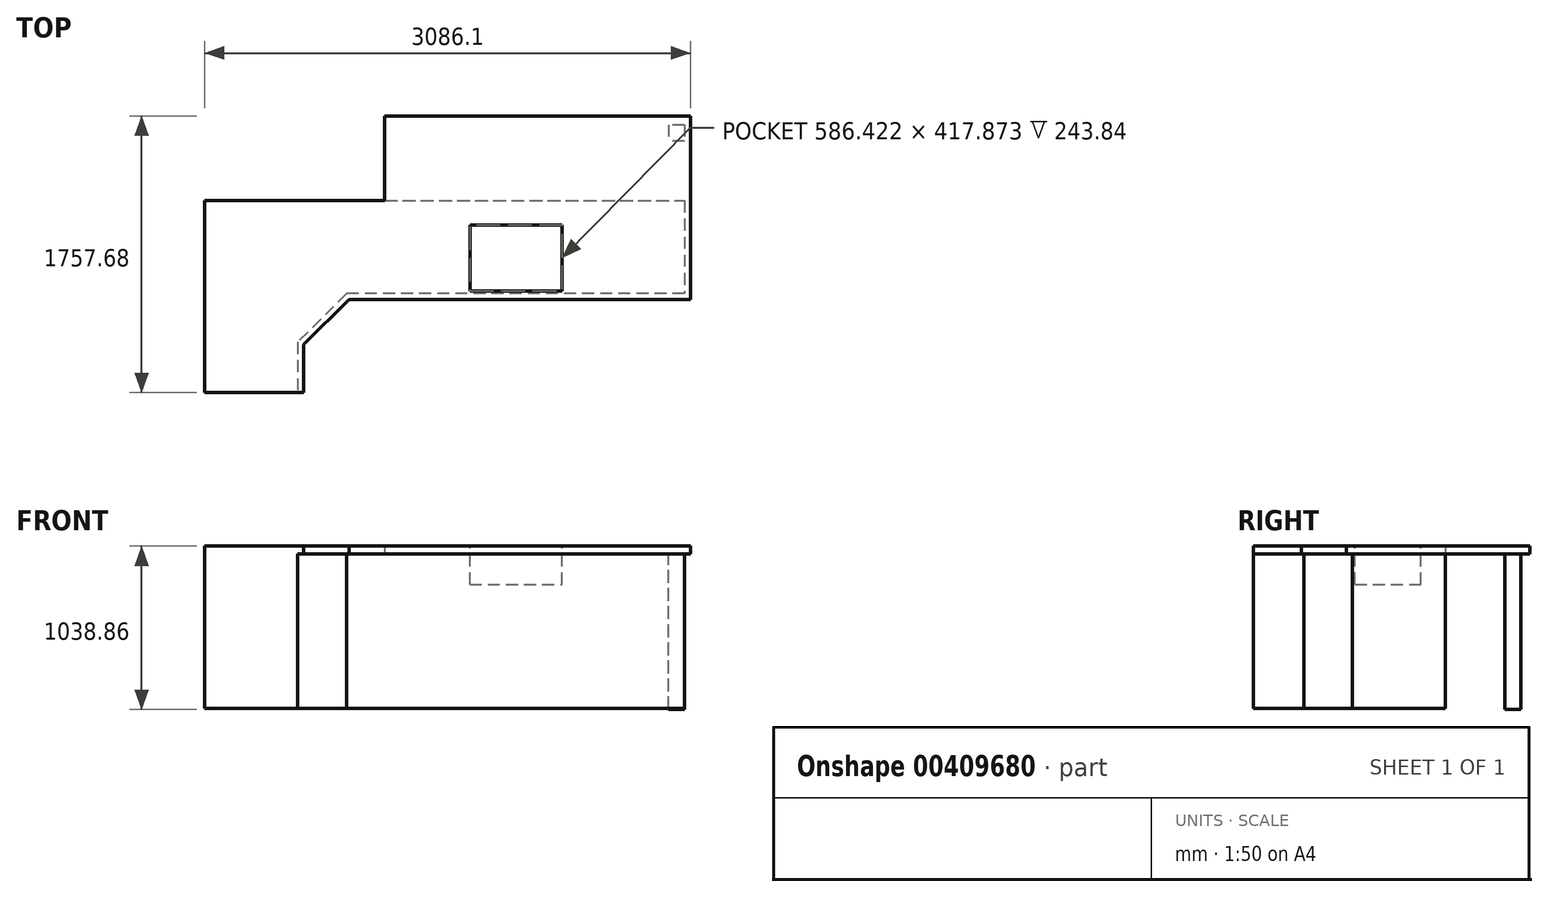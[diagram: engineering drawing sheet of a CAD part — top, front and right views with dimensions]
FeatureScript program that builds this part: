
annotation { "Feature Type Name" : "Feature", "Feature Type Description" : "" }
export const myFeature = defineFeature(function(context is Context, id is Id, definition is map)
    precondition{}
    {
        {
            var Q0;
            Q0=qCreatedBy(makeId("Top.planeOp"),FACE);
            var sketch = newSketch(context, id + "F0", { "sketchPlane" : qUnion([Q0])});
            skLineSegment(sketch, "E0.bottom", {"start": v(0, 0) * mm, "end": v(628.65, 0) * mm});
            skLineSegment(sketch, "E0.top", {"start": v(0, 1219.2) * mm, "end": v(1143, 1219.2) * mm});
            skLineSegment(sketch, "E0.left", {"start": v(0, 0) * mm, "end": v(0, 1219.2) * mm});
            skLineSegment(sketch, "E1", {"start": v(628.65, 0) * mm, "end": v(628.65, 304.8) * mm});
            skLineSegment(sketch, "E2", {"start": v(628.65, 304.8) * mm, "end": v(917.63, 590.55) * mm});
            skLineSegment(sketch, "E3", {"start": v(917.63, 590.55) * mm, "end": v(3086.1, 590.55) * mm});
            skLineSegment(sketch, "E4", {"start": v(1143, 1219.2) * mm, "end": v(1143, 1524) * mm});
            skLineSegment(sketch, "E5", {"start": v(1143, 1524) * mm, "end": v(3086.1, 1524) * mm});
            skLineSegment(sketch, "E6", {"start": v(3086.1, 1524) * mm, "end": v(3086.1, 590.55) * mm});
            skSolve(sketch);
        }
        {
            var Q0;
            Q0=makeQuery(id+"F0.imprint","IMPRINT",FACE,{"disambiguationData":[TD([[makeQuery(id+"F0.imprint","IMPRINT",EDGE,{"derivedFrom":sQuery(id+"F0.wireOp",EDGE,"E0.bottom")}),1.0]])]});
            extrude(context, id + "F1", {"entities" : qUnion([Q0]), "depth" : 50.8 * mm});
        }
        {
            var Q0;
            Q0=makeQuery(id+"F1.opExtrude","CAP_FACE",FACE,{"disambiguationData":[OSD([sQuery(id+"F0.wireOp",EDGE,"E0.bottom"),sQuery(id+"F0.wireOp",EDGE,"E0.top"),sQuery(id+"F0.wireOp",EDGE,"E0.left"),sQuery(id+"F0.wireOp",EDGE,"E1"),sQuery(id+"F0.wireOp",EDGE,"E2"),sQuery(id+"F0.wireOp",EDGE,"E3"),sQuery(id+"F0.wireOp",EDGE,"E4"),sQuery(id+"F0.wireOp",EDGE,"E5"),sQuery(id+"F0.wireOp",EDGE,"E6")])],"isStart":true});
            var sketch = newSketch(context, id + "F2", { "sketchPlane" : qUnion([Q0])});
            skLineSegment(sketch, "E7", {"start": v(1143, -1219.2) * mm, "end": v(3048, -1219.2) * mm});
            skLineSegment(sketch, "E8", {"start": v(3048, -1219.2) * mm, "end": v(3048, -628.65) * mm});
            skLineSegment(sketch, "E9", {"start": v(3048, -628.65) * mm, "end": v(901.97, -628.65) * mm});
            skLineSegment(sketch, "E10", {"start": v(901.97, -628.65) * mm, "end": v(590.55, -320.7) * mm});
            skLineSegment(sketch, "E11", {"start": v(590.55, -320.7) * mm, "end": v(590.55, 0) * mm});
            skLineSegment(sketch, "E12", {"start": v(590.55, 0) * mm, "end": v(0, 0) * mm});
            skLineSegment(sketch, "E13", {"start": v(0, 0) * mm, "end": v(0, -1219.2) * mm});
            skLineSegment(sketch, "E14", {"start": v(0, -1219.2) * mm, "end": v(1143, -1219.2) * mm});
            skSolve(sketch);
        }
        {
            var Q0;
            Q0=makeQuery(id+"F2.imprint","IMPRINT",FACE,{"disambiguationData":[TD([[makeQuery(id+"F2.imprint","IMPRINT",EDGE,{"derivedFrom":sQuery(id+"F2.wireOp",EDGE,"E7")}),1.0]])]});
            extrude(context, id + "F3", {"entities" : qUnion([Q0]), "operationType" : NewBodyOperationType.ADD, "depth" : 980.44 * mm});
        }
        {
            var Q0;
            Q0=makeQuery(id+"F1.opExtrude","SWEPT_FACE",FACE,{"disambiguationData":[OSD([sQuery(id+"F0.wireOp",EDGE,"E5")])]});
            extrude(context, id + "F4", {"entities" : qUnion([Q0]), "operationType" : NewBodyOperationType.ADD, "depth" : 467.36 * mm});
        }
        {
            var Q0;
            {var subQ0=sQuery(id+"F0.wireOp",EDGE,"E5");Q0=makeQuery(id+"F4.boolean.opBoolean","MERGE",FACE,{"derivedFrom":[makeQuery(id+"F1.opExtrude","CAP_FACE",FACE,{"disambiguationData":[OSD([sQuery(id+"F0.wireOp",EDGE,"E0.bottom"),sQuery(id+"F0.wireOp",EDGE,"E0.top"),sQuery(id+"F0.wireOp",EDGE,"E0.left"),sQuery(id+"F0.wireOp",EDGE,"E1"),sQuery(id+"F0.wireOp",EDGE,"E2"),sQuery(id+"F0.wireOp",EDGE,"E3"),sQuery(id+"F0.wireOp",EDGE,"E4"),subQ0,sQuery(id+"F0.wireOp",EDGE,"E6")])],"isStart":true}),makeQuery(id+"F4.opExtrude","SWEPT_FACE",FACE,{"disambiguationData":[OSD([subQ0]),TDD([makeQuery(id+"F1.opExtrude","CAP_EDGE",EDGE,{"disambiguationData":[OSD([subQ0])],"isStart":true})])]})]});}
            var sketch = newSketch(context, id + "F5", { "sketchPlane" : qUnion([Q0])});
            skLineSegment(sketch, "E15", {"start": v(3048, -1219.2) * mm, "end": v(3048, -1700.43) * mm, "construction": true});
            skLineSegment(sketch, "E16.bottom", {"start": v(3048, -1700.43) * mm, "end": v(2946.4, -1700.43) * mm});
            skLineSegment(sketch, "E16.top", {"start": v(3048, -1598.83) * mm, "end": v(2946.4, -1598.83) * mm});
            skLineSegment(sketch, "E16.left", {"start": v(3048, -1700.43) * mm, "end": v(3048, -1598.83) * mm});
            skLineSegment(sketch, "E16.right", {"start": v(2946.4, -1700.43) * mm, "end": v(2946.4, -1598.83) * mm});
            skSolve(sketch);
        }
        {
            var Q0;
            Q0=makeQuery(id+"F5.imprint","IMPRINT",FACE,{"disambiguationData":[TD([[makeQuery(id+"F5.imprint","IMPRINT",EDGE,{"derivedFrom":sQuery(id+"F5.wireOp",EDGE,"E16.bottom")}),-1.0]])]});
            extrude(context, id + "F6", {"entities" : qUnion([Q0]), "operationType" : NewBodyOperationType.ADD, "depth" : 988.06 * mm});
        }
        {
            var Q0;
            {var subQ0=sQuery(id+"F0.wireOp",EDGE,"E5");Q0=makeQuery(id+"F4.boolean.opBoolean","MERGE",FACE,{"derivedFrom":[makeQuery(id+"F1.opExtrude","CAP_FACE",FACE,{"disambiguationData":[OSD([sQuery(id+"F0.wireOp",EDGE,"E0.bottom"),sQuery(id+"F0.wireOp",EDGE,"E0.top"),sQuery(id+"F0.wireOp",EDGE,"E0.left"),sQuery(id+"F0.wireOp",EDGE,"E1"),sQuery(id+"F0.wireOp",EDGE,"E2"),sQuery(id+"F0.wireOp",EDGE,"E3"),sQuery(id+"F0.wireOp",EDGE,"E4"),subQ0,sQuery(id+"F0.wireOp",EDGE,"E6")])],"isStart":false}),makeQuery(id+"F4.opExtrude","SWEPT_FACE",FACE,{"disambiguationData":[OSD([subQ0]),TDD([makeQuery(id+"F1.opExtrude","CAP_EDGE",EDGE,{"disambiguationData":[OSD([subQ0])],"isStart":false})])]})]});}
            var sketch = newSketch(context, id + "F7", { "sketchPlane" : qUnion([Q0])});
            skLineSegment(sketch, "E17.bottom", {"start": v(1684.24, 645.3) * mm, "end": v(2270.66, 645.3) * mm});
            skLineSegment(sketch, "E17.top", {"start": v(1684.24, 1063.18) * mm, "end": v(2270.66, 1063.18) * mm});
            skLineSegment(sketch, "E17.left", {"start": v(1684.24, 645.3) * mm, "end": v(1684.24, 1063.18) * mm});
            skLineSegment(sketch, "E17.right", {"start": v(2270.66, 645.3) * mm, "end": v(2270.66, 1063.18) * mm});
            skSolve(sketch);
        }
        {
            var Q0;
            Q0=makeQuery(id+"F7.imprint","IMPRINT",FACE,{"disambiguationData":[TD([[makeQuery(id+"F7.imprint","IMPRINT",EDGE,{"derivedFrom":sQuery(id+"F7.wireOp",EDGE,"E17.bottom")}),1.0]])]});
            extrude(context, id + "F8", {"entities" : qUnion([Q0]), "operationType" : NewBodyOperationType.REMOVE, "oppositeDirection" : true, "depth" : 243.84 * mm});
        }
        {
            var Q0;
            Q0=makeQuery(id+"F4.opExtrude","CAP_FACE",FACE,{"disambiguationData":[OSD([sQuery(id+"F0.wireOp",EDGE,"E5")])],"isStart":false});
            extrude(context, id + "F9", {"entities" : qUnion([Q0]), "operationType" : NewBodyOperationType.ADD, "oppositeDirection" : true, "depth" : 248.92 * mm});
        }
        {
            var Q0;
            Q0=makeQuery(id+"F4.opExtrude","CAP_FACE",FACE,{"disambiguationData":[OSD([sQuery(id+"F0.wireOp",EDGE,"E5")])],"isStart":false});
            extrude(context, id + "F10", {"entities" : qUnion([Q0]), "operationType" : NewBodyOperationType.REMOVE, "oppositeDirection" : true, "depth" : 233.68 * mm});
        }
    });
